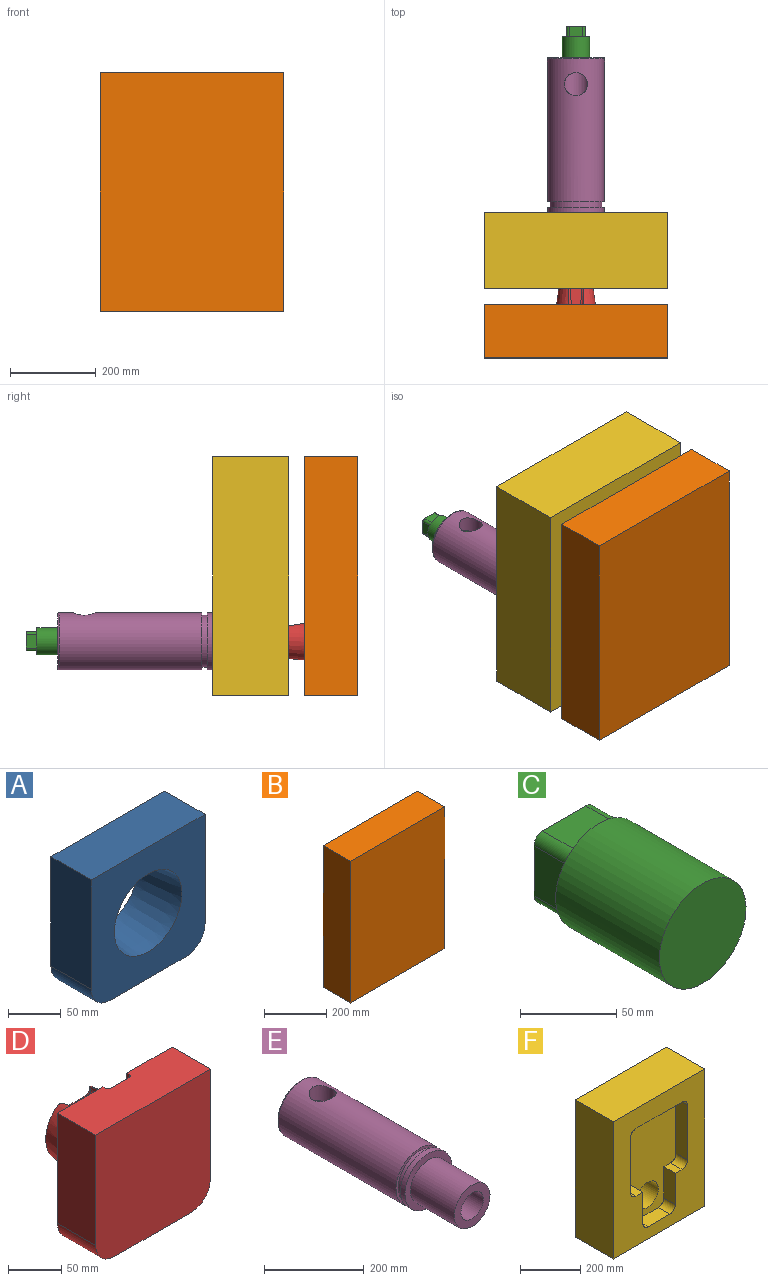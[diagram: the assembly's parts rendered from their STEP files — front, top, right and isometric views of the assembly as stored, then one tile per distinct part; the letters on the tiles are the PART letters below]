
ASSEMBLY  parts=6 mates=5
PART A: 9 faces, bbox 152.4x54x152.4 mm
  f0: plane 127x53.98mm, normal (1,0,0), area 6854.8mm2, adj f1,f4,f5,f8
  f1: plane 152.4x53.98mm, normal (0,0,1), area 8225.8mm2, adj f0,f2,f4,f5
  f2: plane 127x53.98mm, normal (-1,0,0), area 6854.8mm2, adj f1,f4,f5,f7
  f3: plane 101.6x53.98mm, normal (0,0,-1), area 5483.9mm2, adj f4,f5,f7,f8
  f4: plane 152.4x152.4mm, normal (0,1,0), area 18387mm2, adj f0,f1,f2,f3,f6,f7,f8
  f5: plane 152.4x152.4mm, normal (0,-1,0), area 16527mm2, adj f0,f1,f2,f3,f6,f7,f8
  f6: cone r=45.21mm half-angle=7.5deg, axis (0,-1,0), area 14249.9mm2, adj f4,f5
  f7: cylinder r=25.4mm len=53.98mm, axis (0,1,0), area 2153.5mm2, adj f2,f3,f4,f5
  f8: cylinder r=25.4mm len=53.98mm, axis (0,-1,0), area 2153.5mm2, adj f0,f3,f4,f5
PART B: 21 faces, bbox 428.6x123.8x555.6 mm
  f0: plane 555.63x428.63mm, normal (0,1,0), area 142756.2mm2, adj f1,f2,f3,f4,f6,f7,f8,f9
  f1: plane 428.63x123.83mm, normal (0,0,-1), area 53074.5mm2, adj f0,f2,f4,f5
  f2: plane 555.63x123.83mm, normal (1,0,0), area 68800.3mm2, adj f0,f1,f3,f5
  f3: plane 428.63x123.83mm, normal (0,0,1), area 53074.5mm2, adj f0,f2,f4,f5
  f4: plane 555.63x123.83mm, normal (-1,0,0), area 68800.3mm2, adj f0,f1,f3,f5
  f5: plane 555.63x428.63mm, normal (0,-1,0), area 238154.8mm2, adj f1,f2,f3,f4
  f6: plane 127x50.8mm, normal (-1,0,0), area 6451.6mm2, adj f0,f7,f15,f16
  f7: plane 50.8x31.75mm, normal (0,0,1), area 1612.9mm2, adj f0,f6,f16,f17
  f8: plane 222.93x50.8mm, normal (-1,0,0), area 11324.8mm2, adj f0,f16,f17,f18
  f9: plane 215.9x50.8mm, normal (0,0,-1), area 10967.7mm2, adj f0,f16,f18,f19
  f10: plane 222.93x50.8mm, normal (1,0,0), area 11324.8mm2, adj f0,f16,f19,f20
  f11: plane 50.8x31.75mm, normal (0,0,1), area 1612.9mm2, adj f0,f12,f16,f20
  f12: plane 127x50.8mm, normal (1,0,0), area 6451.6mm2, adj f0,f11,f13,f16
  f13: cylinder r=25.4mm len=50.8mm, axis (0,1,0), area 2026.8mm2, adj f0,f12,f14,f16
  f14: plane 101.6x50.8mm, normal (0,0,1), area 5161.3mm2, adj f0,f13,f15,f16
  f15: cylinder r=25.4mm len=50.8mm, axis (0,1,0), area 2026.8mm2, adj f0,f6,f14,f16
  f16: plane 426.13x266.7mm, normal (0,1,0), area 95398.5mm2, adj f6,f7,f8,f9,f10,f11,f12,f13
  f17: cylinder r=25.4mm len=50.8mm, axis (0,-1,0), area 2026.8mm2, adj f0,f7,f8,f16
  f18: cylinder r=25.4mm len=50.8mm, axis (0,1,0), area 2026.8mm2, adj f0,f8,f9,f16
  f19: cylinder r=25.4mm len=50.8mm, axis (0,-1,0), area 2026.8mm2, adj f0,f9,f10,f16
  f20: cylinder r=25.4mm len=50.8mm, axis (0,1,0), area 2026.8mm2, adj f0,f10,f11,f16
PART C: 14 faces, bbox 63.5x101.6x63.5 mm
  f0: cylinder r=31.75mm len=76.2mm, axis (0,-1,0), area 15201.2mm2, adj f1,f2
  f1: plane 63.5x63.5mm, normal (0,1,0), area 1225.7mm2, adj f0,f3,f4,f5,f6,f8,f9,f10
  f2: plane 63.5x63.5mm, normal (0,-1,0), area 3166.9mm2, adj f0
  f3: plane 31.75x25.4mm, normal (-1,0,0), area 806.4mm2, adj f1,f7,f8,f11
  f4: plane 31.75x25.4mm, normal (0,0,1), area 806.4mm2, adj f1,f7,f8,f9
  f5: plane 31.75x25.4mm, normal (1,0,0), area 806.4mm2, adj f1,f7,f9,f10
  f6: plane 31.75x25.4mm, normal (0,0,-1), area 806.4mm2, adj f1,f7,f10,f11
  f7: plane 44.45x44.45mm, normal (0,1,0), area 801.1mm2, adj f3,f4,f5,f6,f8,f9,f10,f11
  f8: cylinder r=6.35mm len=25.4mm, axis (0,1,0), area 253.4mm2, adj f1,f3,f4,f7
  f9: cylinder r=6.35mm len=25.4mm, axis (0,-1,0), area 253.4mm2, adj f1,f4,f5,f7
  f10: cylinder r=6.35mm len=25.4mm, axis (0,1,0), area 253.4mm2, adj f1,f5,f6,f7
  f11: cylinder r=6.35mm len=25.4mm, axis (0,-1,0), area 253.4mm2, adj f1,f3,f6,f7
  f12: cylinder r=19.05mm len=79.5mm, axis (0,1,0), area 9516mm2, adj f7,f13
  f13: plane 38.1x38.1mm, normal (0,1,0), area 1140.1mm2, adj f12
PART D: 31 faces, bbox 152.4x104.8x152.4 mm
  f0: plane 152.4x50.8mm, normal (0,0,1), area 7544.6mm2, adj f13,f14,f16,f17,f20,f21,f22,f26
  f1: cone r=38.1mm half-angle=7.5deg, axis (0,-1,0), area 12258.5mm2, adj f2,f3,f4,f8,f12,f17
  f2: plane 76.2x69.16mm, normal (0,1,0), area 3995.5mm2, adj f1,f8,f9,f10,f11,f12
  f3: plane 50.97x11.56mm, normal (1,0.05,0), area 305.4mm2, adj f1,f6,f12,f17
  f4: plane 50.97x11.56mm, normal (-1,0.05,0), area 305.4mm2, adj f1,f7,f8,f17
  f5: plane 50.97x27.64mm, normal (0,0.05,1), area 1274.2mm2, adj f6,f7,f10,f17
  f6: cylinder r=5.08mm len=51.25mm, axis (0.05,-1,0.05), area 407.5mm2, adj f3,f5,f11,f17
  f7: cylinder r=5.08mm len=51.25mm, axis (-0.05,-1,0.05), area 407.5mm2, adj f4,f5,f9,f17
  f8: cylinder r=3.17mm len=3.17mm, axis (0,0,-1), area 9.1mm2, adj f1,f2,f4,f9
  f9: bspline ~8.24x8.24mm, area 47.1mm2, adj f2,f7,f8,f10
  f10: cylinder r=3.17mm len=27.64mm, axis (1,0,0), area 133.2mm2, adj f2,f5,f9,f11
  f11: bspline ~8.24x8.24mm, area 47.1mm2, adj f2,f6,f10,f12
  f12: cylinder r=3.17mm len=3.17mm, axis (0,0,-1), area 9.1mm2, adj f1,f2,f3,f11
  f13: plane 127x50.8mm, normal (1,0,0), area 6451.6mm2, adj f0,f16,f17,f19
  f14: plane 127x50.8mm, normal (-1,0,0), area 6451.6mm2, adj f0,f16,f17,f18
  f15: plane 101.6x50.8mm, normal (0,0,-1), area 5161.3mm2, adj f16,f17,f18,f19
  f16: plane 152.4x152.4mm, normal (0,-1,0), area 22948.9mm2, adj f0,f13,f14,f15,f18,f19
  f17: plane 152.4x152.4mm, normal (0,1,0), area 15539.4mm2, adj f0,f1,f3,f4,f5,f6,f7,f13
  f18: cylinder r=25.4mm len=50.8mm, axis (0,-1,0), area 2026.8mm2, adj f14,f15,f16,f17
  f19: cylinder r=25.4mm len=50.8mm, axis (0,1,0), area 2026.8mm2, adj f13,f15,f16,f17
  f20: plane 42.42x3.18mm, normal (1,0,0), area 134.7mm2, adj f0,f17,f24,f26
  f21: plane 44.32x25.4mm, normal (0,1,0), area 1124.2mm2, adj f0,f26,f27,f28,f29,f30
  f22: plane 42.42x3.18mm, normal (-1,0,0), area 134.7mm2, adj f0,f17,f25,f30
  f23: plane 21.59x3.18mm, normal (0,0,1), area 68.5mm2, adj f17,f24,f25,f28
  f24: cylinder r=5.08mm len=5.08mm, axis (0,-1,0), area 25.3mm2, adj f17,f20,f23,f27
  f25: cylinder r=5.08mm len=5.08mm, axis (0,1,0), area 25.3mm2, adj f17,f22,f23,f29
  f26: cylinder r=3.17mm len=42.42mm, axis (0,0,-1), area 211.6mm2, adj f0,f20,f21,f27
  f27: torus R=1.91mm, axis (0,-1,0), area 30.8mm2, adj f21,f24,f26,f28
  f28: cylinder r=3.17mm len=21.59mm, axis (1,0,0), area 107.7mm2, adj f21,f23,f27,f29
  f29: torus R=1.91mm, axis (0,-1,0), area 30.8mm2, adj f21,f25,f28,f30
  f30: cylinder r=3.17mm len=42.42mm, axis (0,0,1), area 211.6mm2, adj f0,f21,f22,f29
PART E: 12 faces, bbox 144.3x485.8x144.3 mm
  f0: cylinder r=66.67mm len=333.38mm, axis (0,-1,0), area 137322.9mm2, adj f7,f8,f10
  f1: cylinder r=31.75mm len=485.78mm, axis (0,-1,0), area 94321.5mm2, adj f3,f6,f8
  f2: cylinder r=66.67mm len=133.35mm, axis (0,-1,0), area 5320.4mm2, adj f4,f11
  f3: plane 127x127mm, normal (0,1,0), area 9500.8mm2, adj f1,f7
  f4: plane 133.35x133.35mm, normal (0,-1,0), area 5858.8mm2, adj f2,f5
  f5: cylinder r=50.8mm len=123.83mm, axis (0,1,0), area 39523.2mm2, adj f4,f6
  f6: plane 101.6x101.6mm, normal (0,-1,0), area 4940.4mm2, adj f1,f5
  f7: torus R=63.5mm, axis (0,-1,0), area 2053.2mm2, adj f0,f3
  f8: cylinder r=26.99mm len=53.98mm, axis (0,0,1), area 6616.2mm2, adj f0,f1
  f9: cylinder r=60.32mm len=120.65mm, axis (0,-1,0), area 4813.7mm2, adj f10,f11
  f10: plane 133.35x133.35mm, normal (0,-1,0), area 2533.5mm2, adj f0,f9
  f11: plane 133.35x133.35mm, normal (0,1,0), area 2533.5mm2, adj f2,f9
PART F: 22 faces, bbox 428.6x177.8x555.6 mm
  f0: cylinder r=50.8mm len=123.83mm, axis (0,-1,0), area 39523.2mm2, adj f20,f21
  f1: plane 555.63x428.63mm, normal (0,-1,0), area 142754.4mm2, adj f2,f3,f4,f5,f6,f7,f8,f9
  f2: plane 428.63x177.8mm, normal (0,0,-1), area 76209.5mm2, adj f1,f3,f5,f20
  f3: plane 555.63x177.8mm, normal (1,0,0), area 98790.1mm2, adj f1,f2,f4,f20
  f4: plane 428.63x177.8mm, normal (0,0,1), area 76209.5mm2, adj f1,f3,f5,f20
  f5: plane 555.63x177.8mm, normal (-1,0,0), area 98790.1mm2, adj f1,f2,f4,f20
  f6: plane 53.98x31.75mm, normal (0,0,1), area 1713.7mm2, adj f1,f7,f19,f21
  f7: cylinder r=25.4mm len=53.98mm, axis (0,-1,0), area 2153.5mm2, adj f1,f6,f8,f21
  f8: plane 222.94x53.98mm, normal (-1,0,0), area 12033mm2, adj f1,f7,f9,f21
  f9: cylinder r=25.4mm len=53.98mm, axis (0,-1,0), area 2153.5mm2, adj f1,f8,f10,f21
  f10: plane 215.9x53.98mm, normal (0,0,-1), area 11653.2mm2, adj f1,f9,f11,f21
  f11: cylinder r=25.4mm len=53.98mm, axis (0,-1,0), area 2153.5mm2, adj f1,f10,f12,f21
  f12: plane 222.94x53.98mm, normal (1,0,0), area 12033mm2, adj f1,f11,f13,f21
  f13: cylinder r=25.4mm len=53.98mm, axis (0,-1,0), area 2153.5mm2, adj f1,f12,f14,f21
  f14: plane 53.98x31.75mm, normal (0,0,1), area 1713.7mm2, adj f1,f13,f15,f21
  f15: plane 127x53.98mm, normal (1,0,0), area 6854.8mm2, adj f1,f14,f16,f21
  f16: cylinder r=25.4mm len=53.98mm, axis (0,-1,0), area 2153.5mm2, adj f1,f15,f17,f21
  f17: plane 101.6x53.98mm, normal (0,0,1), area 5483.9mm2, adj f1,f16,f18,f21
  f18: cylinder r=25.4mm len=53.98mm, axis (0,-1,0), area 2153.5mm2, adj f1,f17,f19,f21
  f19: plane 127x53.98mm, normal (-1,0,0), area 6854.8mm2, adj f1,f6,f18,f21
  f20: plane 555.63x428.63mm, normal (0,1,0), area 230047.4mm2, adj f0,f2,f3,f4,f5
  f21: plane 426.14x266.7mm, normal (0,-1,0), area 87293.1mm2, adj f0,f6,f7,f8,f9,f10,f11,f12
PLACE A t=(-342.02,81.86,162.93)mm
PLACE B t=(-342.02,44.52,162.93)mm
PLACE C t=(-342.02,593.79,162.93)mm
PLACE D t=(-342.02,98.5,162.93)mm
PLACE E t=(-342.02,259.66,162.93)mm
PLACE F t=(-342.02,-172.14,162.93)mm
MATE fastened D.f17 <-> B.f0  axis (0,1,0) through (-342.02,44.52,86.73)mm
MATE slider E.f1 <-> C.f0  axis (0,1,0) through (-342.02,621.61,162.93)mm
MATE slider B.f0 <-> F.f1  axis (0,1,0) through (-342.02,44.52,37.51)mm
MATE fastened E.f5 <-> F.f0  axis (0,-1,0) through (-342.02,259.66,162.93)mm
MATE fastened A.f5 <-> F.f1  axis (0,-1,0) through (-342.02,81.86,86.73)mm
